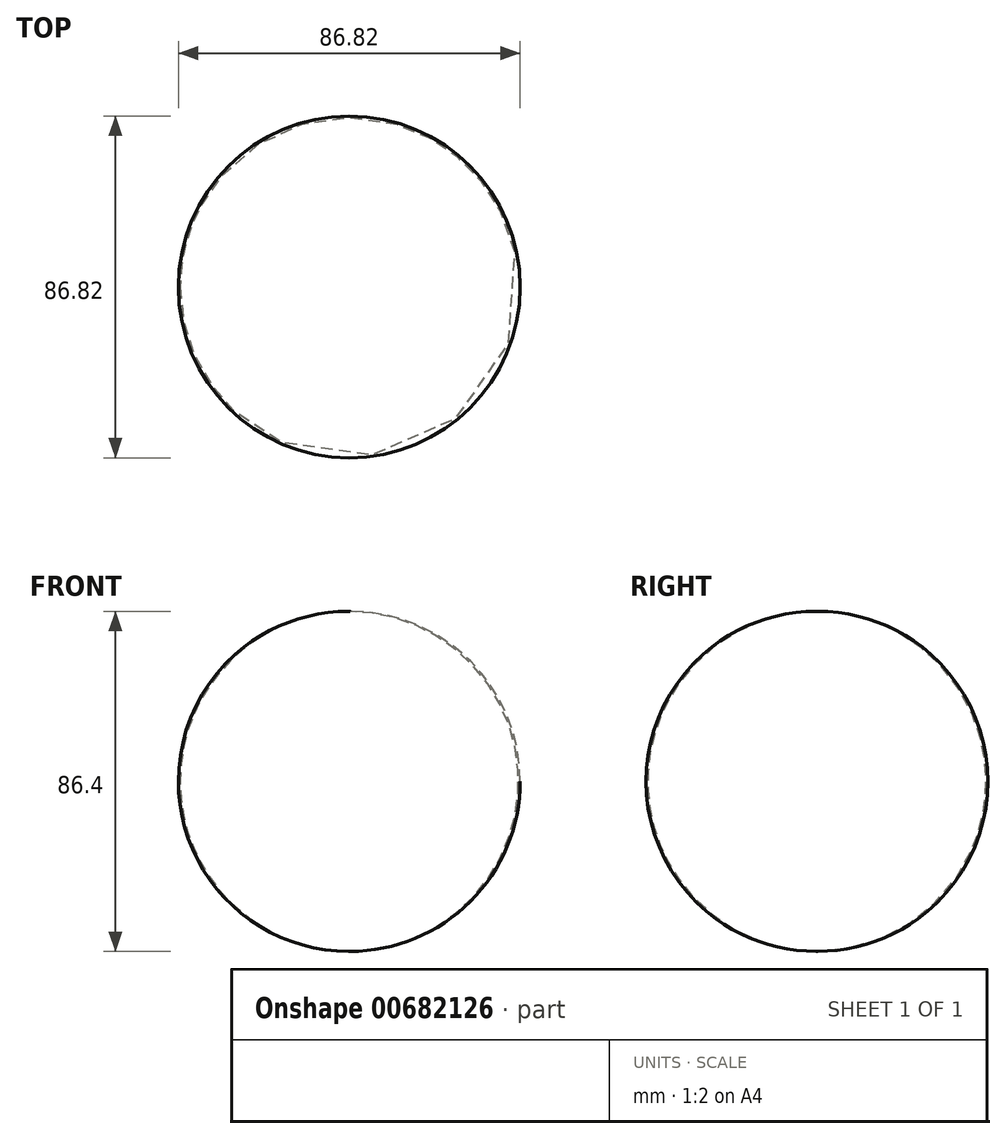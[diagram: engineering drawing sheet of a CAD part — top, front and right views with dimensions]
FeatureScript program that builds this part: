
annotation { "Feature Type Name" : "Feature", "Feature Type Description" : "" }
export const myFeature = defineFeature(function(context is Context, id is Id, definition is map)
    precondition{}
    {
        {
            var Q0;
            Q0=qCreatedBy(makeId("Front.planeOp"),FACE);
            var sketch = newSketch(context, id + "F0", { "sketchPlane" : qUnion([Q0])});
            skLineSegment(sketch, "E0", {"start": v(0, 43.2) * mm, "end": v(0, -43.2) * mm});
            skArc(sketch, "E1", {"start": v(0, 43.2) * mm, "mid": v(-43.41, 0) * mm, "end": v(0, -43.2) * mm});
            skSolve(sketch);
        }
        {
            var Q0;
            Q0=makeQuery(id+"F0.imprint","IMPRINT",FACE,{"disambiguationData":[TD([[makeQuery(id+"F0.imprint","IMPRINT",EDGE,{"derivedFrom":sQuery(id+"F0.wireOp",EDGE,"E0")}),-1.0]])]});
            var Q1;
            Q1=sQuery(id+"F0.wireOp",EDGE,"E0");
            revolve(context, id + "F1", {"entities" : qUnion([Q0]), "axis" : qUnion([Q1]), "revolveType" : RevolveType.FULL});
        }
    });
